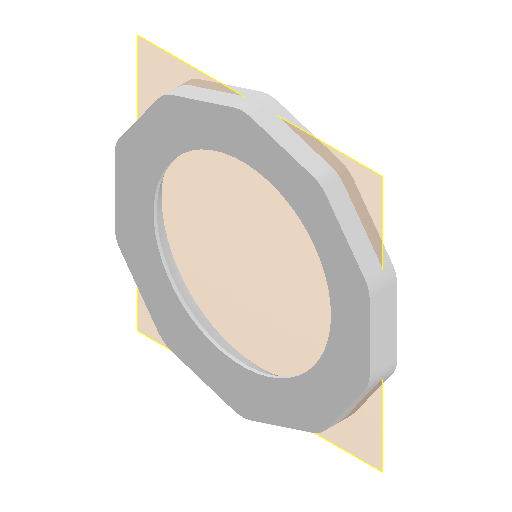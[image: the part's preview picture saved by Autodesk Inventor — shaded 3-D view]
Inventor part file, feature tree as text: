
AUTODESK INVENTOR PART (.ipt)
format: ipt  version: 2022 (Build 260153000, 153)  size: 216,064 bytes
history: native  units: mm
features: reference x5, other x4, extrude x3, sketch x3, projected_geometry x2, plane x1
ambient origin geometry x8: Origin, YZ Plane, XZ Plane, XY Plane, X Axis, Y Axis, Z Axis, Center Point
bodies: Volumenkörper1 (feature_tree)
feature tree (18):
  plane  "Arbeitsebene1"
  extrude  "Extrusion1"  Depth=0.5mm
  extrude  "Extrusion2"  Depth=3.0mm
  extrude  "Extrusion3"  Depth=2.3mm
  sketch  "Skizze1"  dims[d0=5.0mm d1=0.5mm]
  reference  "Referenz1"
  reference  "Referenz2"
  reference  "Referenz3"
  sketch  "Skizze2"  dims[d2=4.5mm d3=0.0mm d4=3.0mm]
  projected_geometry  "Projizierte Kontur1"
  sketch  "Skizze3"  dims[d5=1.0mm d6=0.0mm d7=2.3mm d8=3.0mm d9=0.0mm]
  reference  "Referenz4"
  reference  "Referenz5"
  projected_geometry  "Projizierte Kontur2"
  other  "Anglerfish_bonne_mamman_m12large_v0.iam"
  other  "00_bonne_maman_jar:1"
  other  "Anglerfish_Jar_Adapterplate_v1:1"
  other  "Anglerfish_Lightplate_Tosslink:1"
